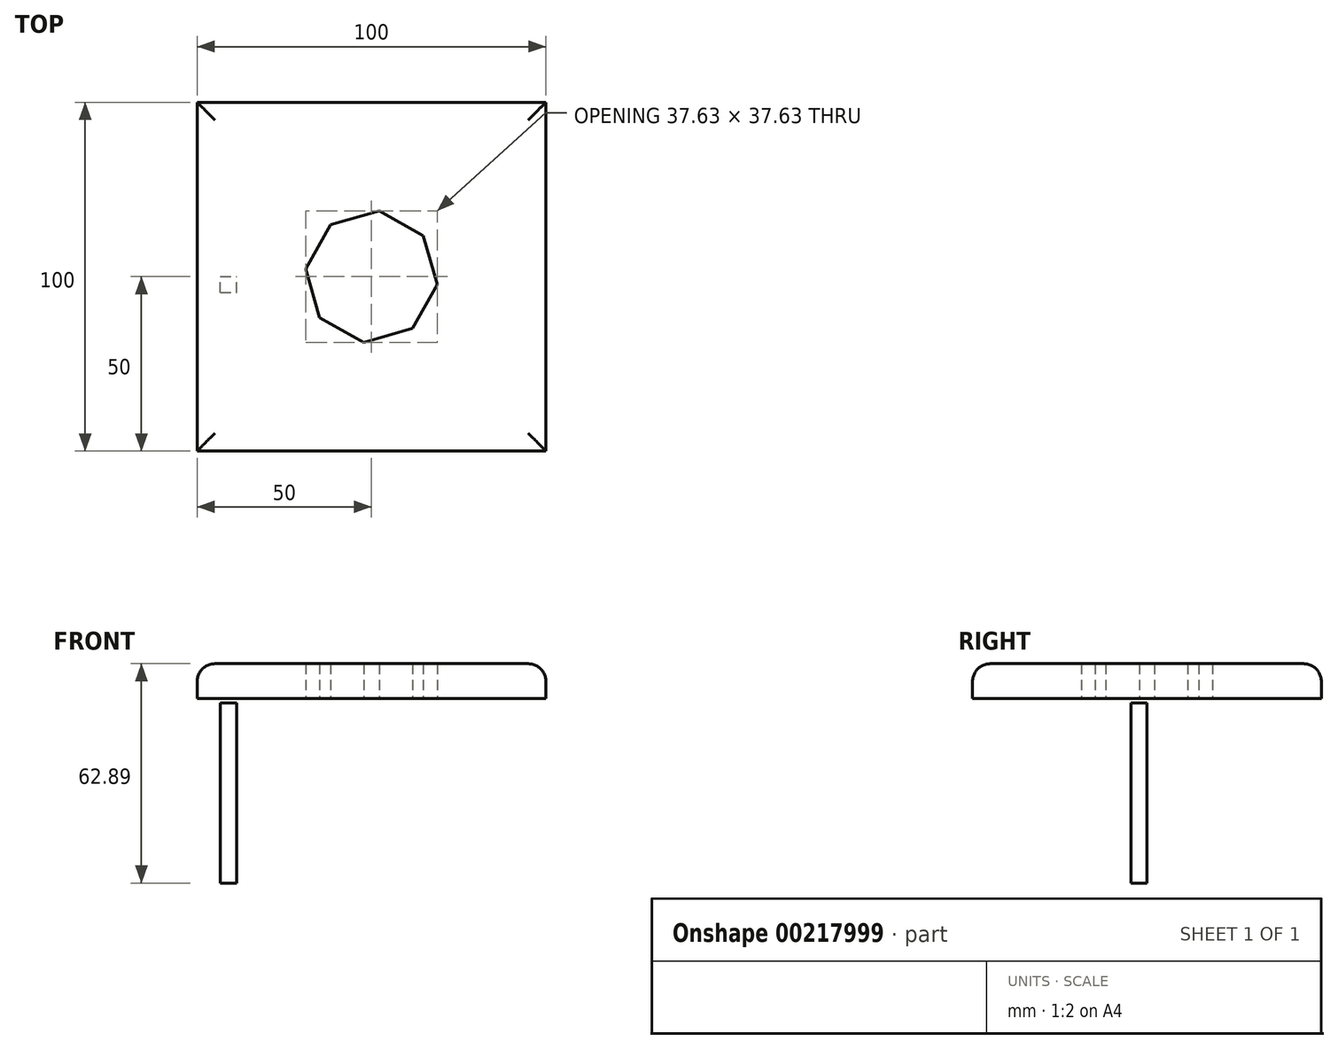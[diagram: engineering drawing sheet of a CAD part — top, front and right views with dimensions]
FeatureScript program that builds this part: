
annotation { "Feature Type Name" : "Feature", "Feature Type Description" : "" }
export const myFeature = defineFeature(function(context is Context, id is Id, definition is map)
    precondition{}
    {
        {
            var Q0;
            Q0=qCreatedBy(makeId("Top.planeOp"),FACE);
            var sketch = newSketch(context, id + "F0", { "sketchPlane" : qUnion([Q0])});
            skLineSegment(sketch, "E0.bottom", {"start": v(-50, 50) * mm, "end": v(50, 50) * mm});
            skLineSegment(sketch, "E0.top", {"start": v(-50, -50) * mm, "end": v(50, -50) * mm});
            skLineSegment(sketch, "E0.left", {"start": v(-50, 50) * mm, "end": v(-50, -50) * mm});
            skLineSegment(sketch, "E0.right", {"start": v(50, 50) * mm, "end": v(50, -50) * mm});
            skPoint(sketch, "E0.middle", {"position": v(0, 0) * mm});
            skSolve(sketch);
        }
        {
            var Q0;
            Q0=makeQuery(id+"F0.imprint","IMPRINT",FACE,{"disambiguationData":[TD([[makeQuery(id+"F0.imprint","IMPRINT",EDGE,{"derivedFrom":sQuery(id+"F0.wireOp",EDGE,"E0.bottom")}),-1.0]])]});
            var sketch = newSketch(context, id + "F1", { "sketchPlane" : qUnion([Q0])});
            skCircle(sketch, "E1.cCircle", {"center": v(0, 0) * mm, "radius": 17.5 * mm, "construction": true});
            skLineSegment(sketch, "E1.0", {"start": v(-18.81, 2.2) * mm, "end": v(-11.75, 14.86) * mm});
            skLineSegment(sketch, "E1.1", {"start": v(-11.75, 14.86) * mm, "end": v(2.2, 18.81) * mm});
            skLineSegment(sketch, "E1.2", {"start": v(2.2, 18.81) * mm, "end": v(14.86, 11.75) * mm});
            skLineSegment(sketch, "E1.3", {"start": v(14.86, 11.75) * mm, "end": v(18.81, -2.2) * mm});
            skLineSegment(sketch, "E1.4", {"start": v(18.81, -2.2) * mm, "end": v(11.75, -14.86) * mm});
            skLineSegment(sketch, "E1.5", {"start": v(11.75, -14.86) * mm, "end": v(-2.2, -18.81) * mm});
            skLineSegment(sketch, "E1.6", {"start": v(-2.2, -18.81) * mm, "end": v(-14.86, -11.75) * mm});
            skLineSegment(sketch, "E1.7", {"start": v(-14.86, -11.75) * mm, "end": v(-18.81, 2.2) * mm});
            skPoint(sketch, "E1.0.midPoint", {"position": v(-15.28, 8.53) * mm});
            skSolve(sketch);
        }
        {
            var Q0;
            Q0=makeQuery(id+"F0.imprint","IMPRINT",FACE,{"disambiguationData":[TD([[makeQuery(id+"F0.imprint","IMPRINT",EDGE,{"derivedFrom":sQuery(id+"F0.wireOp",EDGE,"E0.bottom")}),-1.0]])]});
            extrude(context, id + "F2", {"entities" : qUnion([Q0]), "depth" : 10 * mm});
        }
        {
            var Q0;
            Q0=makeQuery(id+"F2.opExtrude","CAP_FACE",FACE,{"disambiguationData":[OSD([sQuery(id+"F0.wireOp",EDGE,"E0.bottom"),sQuery(id+"F0.wireOp",EDGE,"E0.top"),sQuery(id+"F0.wireOp",EDGE,"E0.left"),sQuery(id+"F0.wireOp",EDGE,"E0.right")])],"isStart":false});
            fillet(context, id + "F3", {"entities" : qUnion([Q0]), "radius" : 5.08 * mm, "tangentPropagation" : true, "allowEdgeOverflow" : false});
        }
        {
            var Q0;
            Q0 = qSketchRegion(id + "F1", true);
            extrude(context, id + "F4", {"entities" : qUnion([Q0]), "operationType" : NewBodyOperationType.REMOVE, "depth" : 61.98 * mm});
        }
        {
            var Q0;
            Q0=qCreatedBy(makeId("Front.planeOp"),FACE);
            var sketch = newSketch(context, id + "F5", { "sketchPlane" : qUnion([Q0])});
            skLineSegment(sketch, "E2.bottom", {"start": v(-43.36, -1.28) * mm, "end": v(-38.7, -1.28) * mm});
            skLineSegment(sketch, "E2.top", {"start": v(-43.36, -52.9) * mm, "end": v(-38.7, -52.9) * mm});
            skLineSegment(sketch, "E2.left", {"start": v(-43.36, -1.28) * mm, "end": v(-43.36, -52.9) * mm});
            skLineSegment(sketch, "E2.right", {"start": v(-38.7, -1.28) * mm, "end": v(-38.7, -52.9) * mm});
            skSolve(sketch);
        }
        {
            var Q0;
            Q0 = qSketchRegion(id + "F5", true);
            extrude(context, id + "F6", {"entities" : qUnion([Q0]), "operationType" : NewBodyOperationType.ADD, "depth" : 4.57 * mm});
        }
    });
